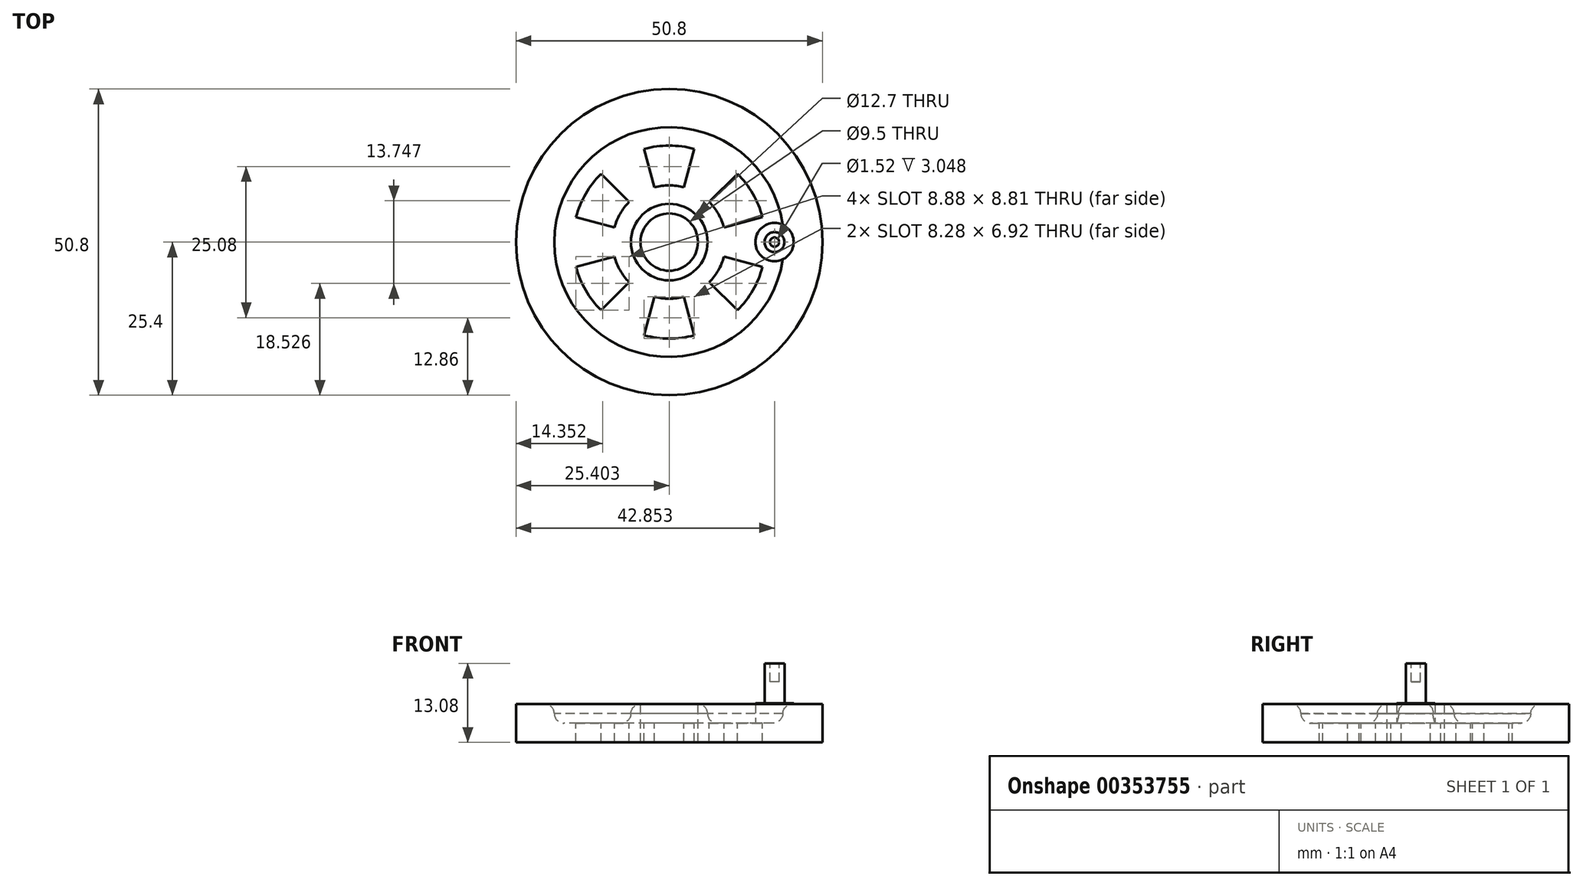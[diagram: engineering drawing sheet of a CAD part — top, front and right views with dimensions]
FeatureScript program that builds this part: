
annotation { "Feature Type Name" : "Feature", "Feature Type Description" : "" }
export const myFeature = defineFeature(function(context is Context, id is Id, definition is map)
    precondition{}
    {
        {
            var Q0;
            Q0=qCreatedBy(makeId("Front.planeOp"),FACE);
            var sketch = newSketch(context, id + "F0", { "sketchPlane" : qUnion([Q0])});
            skLineSegment(sketch, "E0", {"start": v(8.53, 0) * mm, "end": v(8.53, 6.35) * mm});
            skLineSegment(sketch, "E1", {"start": v(8.53, 6.35) * mm, "end": v(8.53, 6.35) * mm});
            skLineSegment(sketch, "E2", {"start": v(10.13, 4.78) * mm, "end": v(10.13, 4.75) * mm});
            skLineSegment(sketch, "E3", {"start": v(11.73, 3.18) * mm, "end": v(21.23, 3.18) * mm});
            skLineSegment(sketch, "E4", {"start": v(22.83, 4.75) * mm, "end": v(22.83, 4.78) * mm});
            skLineSegment(sketch, "E5", {"start": v(24.43, 6.35) * mm, "end": v(29.18, 6.35) * mm});
            skLineSegment(sketch, "E6", {"start": v(29.18, 6.35) * mm, "end": v(29.18, 0) * mm});
            skLineSegment(sketch, "E7", {"start": v(29.18, 0) * mm, "end": v(8.53, 0) * mm});
            skArc(sketch, "E8", {"start": v(29.18, 6.35) * mm, "mid": v(32.36, 3.18) * mm, "end": v(29.18, 0) * mm});
            skLineSegment(sketch, "E9", {"start": v(3.78, 8.27) * mm, "end": v(3.78, -3.55) * mm, "construction": true});
            skPoint(sketch, "E10.visualSharp", {"position": v(10.13, 6.35) * mm});
            skArc(sketch, "E10.filletArc", {"start": v(10.13, 4.75) * mm, "mid": v(9.66, 5.88) * mm, "end": v(8.53, 6.35) * mm});
            skPoint(sketch, "E11.visualSharp", {"position": v(10.13, 3.18) * mm});
            skArc(sketch, "E11.filletArc", {"start": v(10.13, 4.78) * mm, "mid": v(10.6, 3.64) * mm, "end": v(11.73, 3.18) * mm});
            skPoint(sketch, "E12.visualSharp", {"position": v(22.83, 6.35) * mm});
            skArc(sketch, "E12.filletArc", {"start": v(24.43, 6.35) * mm, "mid": v(23.3, 5.88) * mm, "end": v(22.83, 4.75) * mm});
            skPoint(sketch, "E13.visualSharp", {"position": v(22.83, 3.18) * mm});
            skArc(sketch, "E13.filletArc", {"start": v(21.23, 3.18) * mm, "mid": v(22.36, 3.64) * mm, "end": v(22.83, 4.78) * mm});
            skSolve(sketch);
        }
        {
            var Q0;
            Q0=makeQuery(id+"F0.imprint","IMPRINT",FACE,{"disambiguationData":[TD([[makeQuery(id+"F0.imprint","IMPRINT",EDGE,{"derivedFrom":sQuery(id+"F0.wireOp",EDGE,"E0")}),-1.0]])]});
            var Q1;
            Q1=sQuery(id+"F0.wireOp",EDGE,"E9");
            revolve(context, id + "F1", {"entities" : qUnion([Q0]), "axis" : qUnion([Q1]), "revolveType" : RevolveType.FULL});
        }
        {
            var Q0;
            Q0=makeQuery(id+"F1.opRevolve","SWEPT_FACE",FACE,{"disambiguationData":[OSD([sQuery(id+"F0.wireOp",EDGE,"E3")])]});
            var sketch = newSketch(context, id + "F2", { "sketchPlane" : qUnion([Q0])});
            skLineSegment(sketch, "E14", {"start": v(6.22, 9.08) * mm, "end": v(7.92, 15.46) * mm});
            skLineSegment(sketch, "E15.MirrorCS", {"start": v(1.35, 9.08) * mm, "end": v(-0.36, 15.46) * mm});
            skArc(sketch, "E16", {"start": v(7.92, 15.46) * mm, "mid": v(3.78, 16) * mm, "end": v(-0.36, 15.46) * mm});
            skArc(sketch, "E17", {"start": v(6.22, 9.08) * mm, "mid": v(3.78, 9.4) * mm, "end": v(1.35, 9.08) * mm});
            skPoint(sketch, "E18.orphan", {"position": v(-0.73, 16.86) * mm});
            skPoint(sketch, "E19.orphan", {"position": v(8.3, 16.86) * mm});
            skArc(sketch, "E20.1.0", {"start": v(-7.53, 11.32) * mm, "mid": v(-10.08, 8) * mm, "end": v(-11.67, 4.14) * mm});
            skLineSegment(sketch, "E20.1.1", {"start": v(-5.3, 2.43) * mm, "end": v(-11.67, 4.14) * mm});
            skArc(sketch, "E20.1.2", {"start": v(-2.86, 6.65) * mm, "mid": v(-4.36, 4.7) * mm, "end": v(-5.3, 2.43) * mm});
            skLineSegment(sketch, "E20.1.3", {"start": v(-2.86, 6.65) * mm, "end": v(-7.53, 11.32) * mm});
            skArc(sketch, "E20.2.0", {"start": v(-11.67, -4.14) * mm, "mid": v(-10.08, -8) * mm, "end": v(-7.53, -11.32) * mm});
            skLineSegment(sketch, "E20.2.1", {"start": v(-2.86, -6.65) * mm, "end": v(-7.53, -11.32) * mm});
            skArc(sketch, "E20.2.2", {"start": v(-5.3, -2.43) * mm, "mid": v(-4.36, -4.7) * mm, "end": v(-2.86, -6.65) * mm});
            skLineSegment(sketch, "E20.2.3", {"start": v(-5.3, -2.43) * mm, "end": v(-11.67, -4.14) * mm});
            skArc(sketch, "E20.3.0", {"start": v(-0.36, -15.46) * mm, "mid": v(3.78, -16) * mm, "end": v(7.92, -15.46) * mm});
            skLineSegment(sketch, "E20.3.1", {"start": v(6.22, -9.08) * mm, "end": v(7.92, -15.46) * mm});
            skArc(sketch, "E20.3.2", {"start": v(1.35, -9.08) * mm, "mid": v(3.78, -9.4) * mm, "end": v(6.22, -9.08) * mm});
            skLineSegment(sketch, "E20.3.3", {"start": v(1.35, -9.08) * mm, "end": v(-0.36, -15.46) * mm});
            skArc(sketch, "E20.4.0", {"start": v(15.1, -11.32) * mm, "mid": v(17.64, -8) * mm, "end": v(19.24, -4.14) * mm});
            skLineSegment(sketch, "E20.4.1", {"start": v(12.86, -2.43) * mm, "end": v(19.24, -4.14) * mm});
            skArc(sketch, "E20.4.2", {"start": v(10.43, -6.65) * mm, "mid": v(11.92, -4.7) * mm, "end": v(12.86, -2.43) * mm});
            skLineSegment(sketch, "E20.4.3", {"start": v(10.43, -6.65) * mm, "end": v(15.1, -11.32) * mm});
            skArc(sketch, "E21.1.5.0", {"start": v(19.24, 4.14) * mm, "mid": v(17.64, 8) * mm, "end": v(15.1, 11.32) * mm});
            skLineSegment(sketch, "E21.4.5.0", {"start": v(10.43, 6.65) * mm, "end": v(15.1, 11.32) * mm});
            skArc(sketch, "E21.7.5.0", {"start": v(12.86, 2.43) * mm, "mid": v(11.92, 4.7) * mm, "end": v(10.43, 6.65) * mm});
            skLineSegment(sketch, "E21.11.5.0", {"start": v(12.86, 2.43) * mm, "end": v(19.24, 4.14) * mm});
            skSolve(sketch);
        }
        {
            var Q0;
            Q0=makeQuery(id+"F2.imprint","IMPRINT",FACE,{"disambiguationData":[TD([[makeQuery(id+"F2.imprint","IMPRINT",EDGE,{"derivedFrom":sQuery(id+"F2.wireOp",EDGE,"E14")}),1.0]])]});
            var Q1;
            Q1=makeQuery(id+"F2.imprint","IMPRINT",FACE,{"disambiguationData":[TD([[makeQuery(id+"F2.imprint","IMPRINT",EDGE,{"derivedFrom":sQuery(id+"F2.wireOp",EDGE,"E20.1.0")}),1.0]])]});
            var Q2;
            Q2=makeQuery(id+"F2.imprint","IMPRINT",FACE,{"disambiguationData":[TD([[makeQuery(id+"F2.imprint","IMPRINT",EDGE,{"derivedFrom":sQuery(id+"F2.wireOp",EDGE,"E20.2.0")}),1.0]])]});
            var Q3;
            Q3=makeQuery(id+"F2.imprint","IMPRINT",FACE,{"disambiguationData":[TD([[makeQuery(id+"F2.imprint","IMPRINT",EDGE,{"derivedFrom":sQuery(id+"F2.wireOp",EDGE,"E20.3.0")}),1.0]])]});
            var Q4;
            Q4=makeQuery(id+"F2.imprint","IMPRINT",FACE,{"disambiguationData":[TD([[makeQuery(id+"F2.imprint","IMPRINT",EDGE,{"derivedFrom":sQuery(id+"F2.wireOp",EDGE,"E20.4.0")}),1.0]])]});
            var Q5;
            Q5=makeQuery(id+"F2.imprint","IMPRINT",FACE,{"disambiguationData":[TD([[makeQuery(id+"F2.imprint","IMPRINT",EDGE,{"derivedFrom":sQuery(id+"F2.wireOp",EDGE,"E21.1.5.0")}),1.0]])]});
            extrude(context, id + "F3", {"entities" : qUnion([Q0, Q1, Q2, Q3, Q4, Q5]), "operationType" : NewBodyOperationType.REMOVE, "oppositeDirection" : true, "depth" : 25.4 * mm});
        }
        {
            var Q0;
            Q0=makeQuery(id+"F1.opRevolve","SWEPT_BODY",BODY,{"disambiguationData":[OSD([sQuery(id+"F0.wireOp",EDGE,"E0"),sQuery(id+"F0.wireOp",EDGE,"E2"),sQuery(id+"F0.wireOp",EDGE,"E3"),sQuery(id+"F0.wireOp",EDGE,"E4"),sQuery(id+"F0.wireOp",EDGE,"E5"),sQuery(id+"F0.wireOp",EDGE,"E6"),sQuery(id+"F0.wireOp",EDGE,"E7"),sQuery(id+"F0.wireOp",EDGE,"E10.filletArc"),sQuery(id+"F0.wireOp",EDGE,"E11.filletArc"),sQuery(id+"F0.wireOp",EDGE,"E12.filletArc"),sQuery(id+"F0.wireOp",EDGE,"E13.filletArc")])]});
            var Q1;
            Q1=makeQuery(id+"F1.opRevolve","SWEPT_EDGE",EDGE,{"disambiguationData":[OSD([sQuery(id+"F0.wireOp",EDGE,"E5"),sQuery(id+"F0.wireOp",EDGE,"E6"),sQuery(id+"F0.wireOp",EDGE,"E8")])]});
            var Q2;
            Q2=qCreatedBy(makeId("Right.planeOp"),FACE);
            transform(context, id + "F4", {"entities" : qUnion([Q0]), "transformType" : TransformType.TRANSLATION_DISTANCE, "transformDirection" : qUnion([Q2]), "distance" : 3.8 * mm, "oppositeDirection" : true, "makeCopy" : false});
        }
        {
            var Q0;
            Q0=makeQuery(id+"F1.opRevolve","SWEPT_FACE",FACE,{"disambiguationData":[OSD([sQuery(id+"F0.wireOp",EDGE,"E3")])]});
            var sketch = newSketch(context, id + "F5", { "sketchPlane" : qUnion([Q0])});
            skCircle(sketch, "E22", {"center": v(17.42, 0) * mm, "radius": 3.18 * mm});
            skSolve(sketch);
        }
        {
            var Q0;
            Q0 = qSketchRegion(id + "F5", true);
            extrude(context, id + "F6", {"entities" : qUnion([Q0]), "operationType" : NewBodyOperationType.ADD, "depth" : 3.3 * mm});
        }
        {
            var Q0;
            Q0=makeQuery(id+"F6.opExtrude","CAP_FACE",FACE,{"disambiguationData":[OSD([sQuery(id+"F5.wireOp",EDGE,"E22")])],"isStart":false});
            var sketch = newSketch(context, id + "F7", { "sketchPlane" : qUnion([Q0])});
            skCircle(sketch, "E23", {"center": v(17.42, 0) * mm, "radius": 1.65 * mm});
            skSolve(sketch);
        }
        {
            var Q0;
            Q0=makeQuery(id+"F7.imprint","IMPRINT",FACE,{"disambiguationData":[TD([[makeQuery(id+"F7.imprint","IMPRINT",EDGE,{"derivedFrom":sQuery(id+"F7.wireOp",EDGE,"E23")}),1.0]])]});
            var Q1;
            Q1=sQuery(id+"F7.wireOp",EDGE,"E23");
            extrude(context, id + "F8", {"entities" : qUnion([Q0]), "surfaceEntities" : qUnion([Q1]), "depth" : 6.6 * mm});
        }
        {
            var Q0;
            Q0=makeQuery(id+"F8.opExtrude","CAP_FACE",FACE,{"disambiguationData":[OSD([sQuery(id+"F7.wireOp",EDGE,"E23")])],"isStart":false});
            var sketch = newSketch(context, id + "F9", { "sketchPlane" : qUnion([Q0])});
            skCircle(sketch, "E24", {"center": v(17.42, 0) * mm, "radius": 0.76 * mm});
            skSolve(sketch);
        }
        {
            var Q0;
            Q0=makeQuery(id+"F9.imprint","IMPRINT",FACE,{"disambiguationData":[TD([[makeQuery(id+"F9.imprint","IMPRINT",EDGE,{"derivedFrom":sQuery(id+"F9.wireOp",EDGE,"E24")}),1.0]])]});
            extrude(context, id + "F10", {"entities" : qUnion([Q0]), "operationType" : NewBodyOperationType.REMOVE, "oppositeDirection" : true, "depth" : 3.05 * mm});
        }
    });
